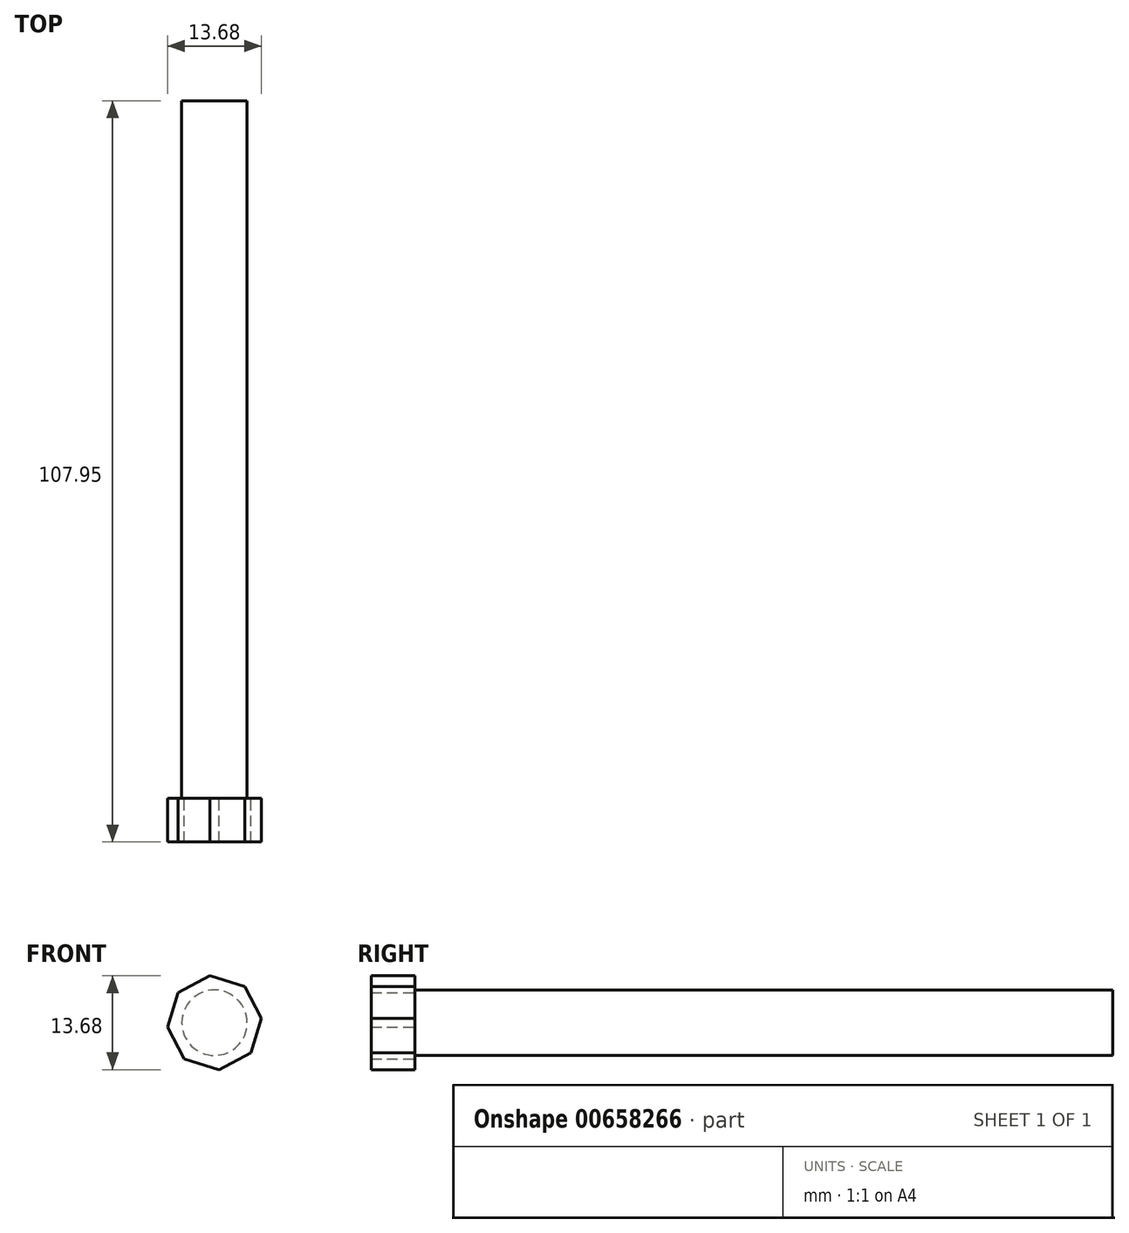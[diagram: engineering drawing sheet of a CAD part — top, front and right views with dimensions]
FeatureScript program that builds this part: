
annotation { "Feature Type Name" : "Feature", "Feature Type Description" : "" }
export const myFeature = defineFeature(function(context is Context, id is Id, definition is map)
    precondition{}
    {
        {
            var Q0;
            Q0=qCreatedBy(makeId("Front.planeOp"),FACE);
            var sketch = newSketch(context, id + "F0", { "sketchPlane" : qUnion([Q0])});
            skCircle(sketch, "E0.cCircle", {"center": v(0, 0) * mm, "radius": 6.35 * mm, "construction": true});
            skLineSegment(sketch, "E0.0", {"start": v(4.39, 5.3) * mm, "end": v(6.84, 0.64) * mm});
            skLineSegment(sketch, "E0.1", {"start": v(6.84, 0.64) * mm, "end": v(5.3, -4.39) * mm});
            skLineSegment(sketch, "E0.2", {"start": v(5.3, -4.39) * mm, "end": v(0.64, -6.84) * mm});
            skLineSegment(sketch, "E0.3", {"start": v(0.64, -6.84) * mm, "end": v(-4.39, -5.3) * mm});
            skLineSegment(sketch, "E0.4", {"start": v(-4.39, -5.3) * mm, "end": v(-6.84, -0.64) * mm});
            skLineSegment(sketch, "E0.5", {"start": v(-6.84, -0.64) * mm, "end": v(-5.3, 4.39) * mm});
            skLineSegment(sketch, "E0.6", {"start": v(-5.3, 4.39) * mm, "end": v(-0.64, 6.84) * mm});
            skLineSegment(sketch, "E0.7", {"start": v(-0.64, 6.84) * mm, "end": v(4.39, 5.3) * mm});
            skPoint(sketch, "E0.0.midPoint", {"position": v(5.61, 2.97) * mm});
            skSolve(sketch);
        }
        {
            var Q0;
            Q0=qCreatedBy(makeId("Front.planeOp"),FACE);
            var sketch = newSketch(context, id + "F1", { "sketchPlane" : qUnion([Q0])});
            skCircle(sketch, "E1", {"center": v(0, 0) * mm, "radius": 4.76 * mm});
            skSolve(sketch);
        }
        {
            var Q0;
            Q0 = qSketchRegion(id + "F1", true);
            extrude(context, id + "F2", {"entities" : qUnion([Q0]), "oppositeDirection" : true, "depth" : 101.6 * mm, "offsetDistance" : 25.4 * mm});
        }
        {
            var Q0;
            Q0 = qSketchRegion(id + "F0", true);
            extrude(context, id + "F3", {"entities" : qUnion([Q0]), "operationType" : NewBodyOperationType.ADD, "depth" : 6.35 * mm, "offsetDistance" : 25.4 * mm});
        }
    });
